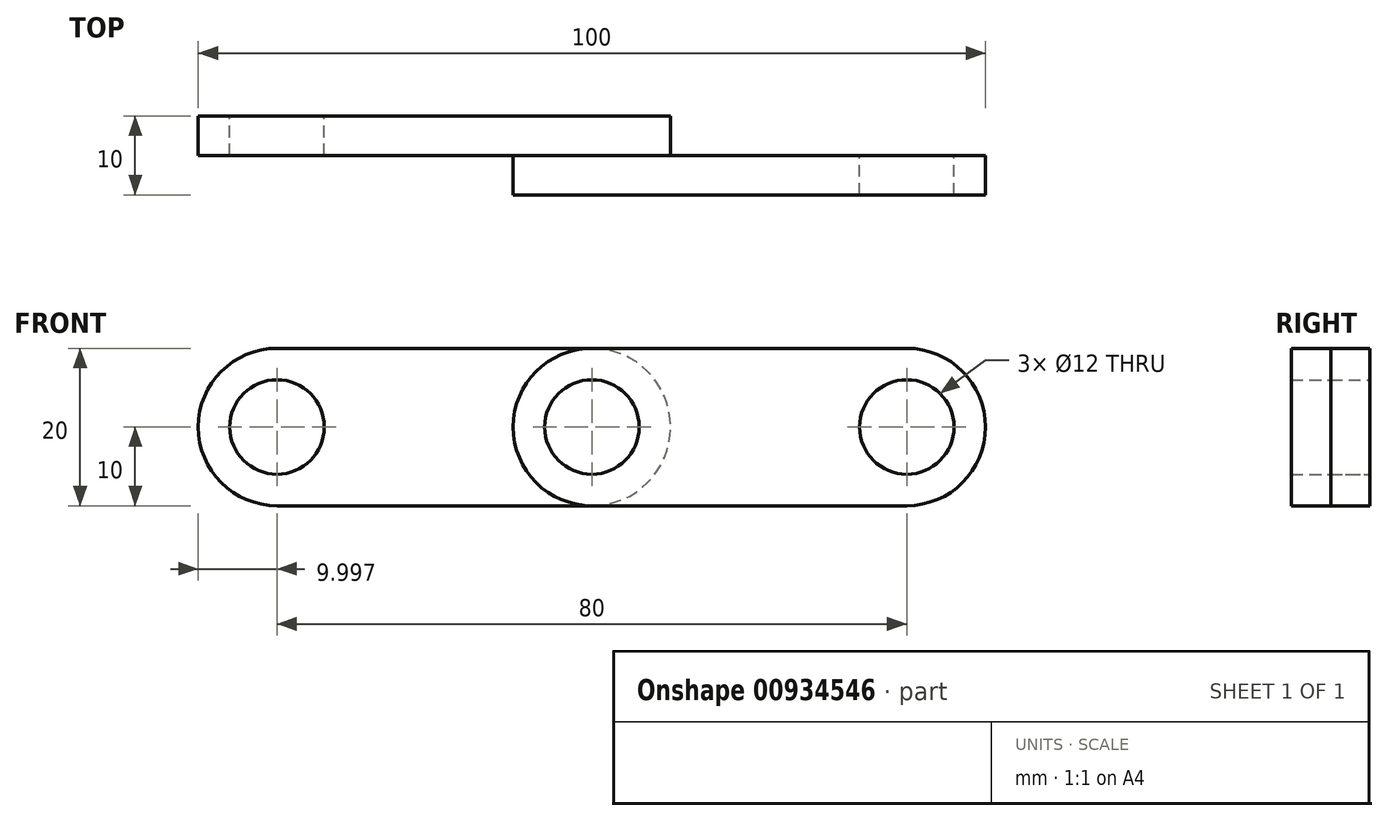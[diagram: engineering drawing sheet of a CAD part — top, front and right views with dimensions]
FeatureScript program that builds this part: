
annotation { "Feature Type Name" : "Feature", "Feature Type Description" : "" }
export const myFeature = defineFeature(function(context is Context, id is Id, definition is map)
    precondition{}
    {
        {
            var Q0;
            Q0=qCreatedBy(makeId("Front.planeOp"),FACE);
            var sketch = newSketch(context, id + "F0", { "sketchPlane" : qUnion([Q0])});
            skLineSegment(sketch, "E0", {"start": v(-48.47, 0) * mm, "end": v(-8.47, 0) * mm, "construction": true});
            skLineSegment(sketch, "E1", {"start": v(-48.47, -10) * mm, "end": v(-48.47, -10) * mm});
            skLineSegment(sketch, "E2", {"start": v(-8.47, 10) * mm, "end": v(-48.47, 10) * mm});
            skLineSegment(sketch, "E3", {"start": v(-48.47, -10) * mm, "end": v(-8.47, -10) * mm});
            skArc(sketch, "E4", {"start": v(-8.47, -10) * mm, "mid": v(1.53, 0) * mm, "end": v(-8.47, 10) * mm});
            skArc(sketch, "E5", {"start": v(-48.47, 10) * mm, "mid": v(-58.47, 0) * mm, "end": v(-48.47, -10) * mm});
            skCircle(sketch, "E6", {"center": v(-48.47, 0) * mm, "radius": 6 * mm});
            skCircle(sketch, "E7", {"center": v(-8.47, 0) * mm, "radius": 6 * mm});
            skSolve(sketch);
        }
        {
            var Q0;
            Q0 = qSketchRegion(id + "F0", true);
            extrude(context, id + "F1", {"entities" : qUnion([Q0]), "depth" : 5 * mm, "offsetDistance" : 25 * mm});
        }
        {
            var Q0;
            Q0=makeQuery(id+"F1.opExtrude","CAP_FACE",FACE,{"disambiguationData":[OSD([sQuery(id+"F0.wireOp",EDGE,"E2"),sQuery(id+"F0.wireOp",EDGE,"E3"),sQuery(id+"F0.wireOp",EDGE,"E4"),sQuery(id+"F0.wireOp",EDGE,"E5"),sQuery(id+"F0.wireOp",EDGE,"E6"),sQuery(id+"F0.wireOp",EDGE,"E7")])],"isStart":false});
            var sketch = newSketch(context, id + "F2", { "sketchPlane" : qUnion([Q0])});
            skLineSegment(sketch, "E8", {"start": v(-8.47, 0) * mm, "end": v(31.53, 0) * mm, "construction": true});
            skLineSegment(sketch, "E9", {"start": v(-8.47, -10) * mm, "end": v(-8.47, -10) * mm});
            skLineSegment(sketch, "E10", {"start": v(31.53, 10) * mm, "end": v(-8.47, 10) * mm});
            skLineSegment(sketch, "E11", {"start": v(-8.47, -10) * mm, "end": v(31.53, -10) * mm});
            skArc(sketch, "E12", {"start": v(31.53, -10) * mm, "mid": v(41.53, 0) * mm, "end": v(31.53, 10) * mm});
            skArc(sketch, "E13", {"start": v(-8.47, 10) * mm, "mid": v(-18.47, 0) * mm, "end": v(-8.47, -10) * mm});
            skCircle(sketch, "E14", {"center": v(-8.47, 0) * mm, "radius": 6 * mm});
            skCircle(sketch, "E15", {"center": v(31.53, 0) * mm, "radius": 6 * mm});
            skSolve(sketch);
        }
        {
            var Q0;
            Q0 = qSketchRegion(id + "F2", true);
            extrude(context, id + "F3", {"entities" : qUnion([Q0]), "operationType" : NewBodyOperationType.ADD, "depth" : 5 * mm, "offsetDistance" : 25 * mm});
        }
        {
            var Q0;
            Q0=qCreatedBy(makeId("Top.planeOp"),FACE);
            var sketch = newSketch(context, id + "F4", { "sketchPlane" : qUnion([Q0])});
            skLineSegment(sketch, "E16", {"start": v(29.91, 29.91) * mm, "end": v(29.91, 71.72) * mm, "construction": true});
            skLineSegment(sketch, "E17", {"start": v(23.91, 61.72) * mm, "end": v(23.91, 41.72) * mm});
            skLineSegment(sketch, "E18", {"start": v(23.91, 61.72) * mm, "end": v(18.91, 61.72) * mm});
            skLineSegment(sketch, "E19", {"start": v(23.91, 41.72) * mm, "end": v(18.91, 41.72) * mm});
            skArc(sketch, "E20", {"start": v(29.91, 71.72) * mm, "mid": v(23.14, 68.12) * mm, "end": v(18.91, 61.72) * mm});
            skArc(sketch, "E21", {"start": v(18.91, 41.72) * mm, "mid": v(22.68, 34.2) * mm, "end": v(29.91, 29.91) * mm});
            skSolve(sketch);
        }
        {
            var Q0;
            Q0=sQuery(id+"F4.wireOp",EDGE,"E20");
            var Q1;
            Q1=sQuery(id+"F4.wireOp",EDGE,"E17");
            var Q2;
            Q2=sQuery(id+"F4.wireOp",EDGE,"E21");
            var Q3;
            Q3=sQuery(id+"F4.wireOp",EDGE,"E18");
            var Q4;
            Q4=sQuery(id+"F4.wireOp",EDGE,"E19");
            var Q5;
            Q5=sQuery(id+"F4.wireOp",EDGE,"E16");
            revolve(context, id + "F5", {"bodyType" : ToolBodyType.SURFACE, "surfaceOperationType" : NewSurfaceOperationType.NEW, "surfaceEntities" : qUnion([Q0, Q1, Q2, Q3, Q4]), "axis" : qUnion([Q5]), "revolveType" : RevolveType.FULL});
        }
    });
